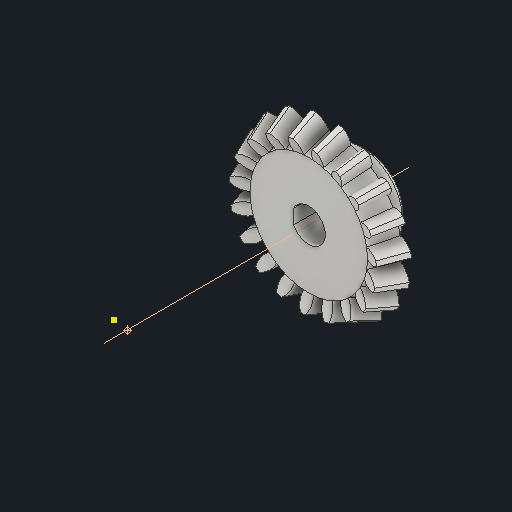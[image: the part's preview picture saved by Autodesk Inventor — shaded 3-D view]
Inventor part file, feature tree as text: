
AUTODESK INVENTOR PART (.ipt)
format: ipt  version: 2022 (Build 260153000, 153)  size: 597,504 bytes
history: native  units: mm
features: other x24, sketch x5, extrude x3, loft x2, pattern_circular x2, chamfer x1
ambient origin geometry x6: Origin, XZ Plane, X Axis, Y Axis, Z Axis, Center Point
bodies: Solid1 (feature_tree)
feature tree (37):
  other  "Top Point"
  other  "Mesh Plane2"
  other  "Teeth Body"
  other  "Start Point"
  other  "Tooth Plane"
  other  "Start Sketch"
  other  "End Point"
  other  "3D Sketch Right"
  other  "End Plane Right"
  loft  "Loft Right"
  pattern_circular  "Circular Pattern Right"  [2 undecoded]
  other  "3D Sketch Left"
  other  "End Plane Left"
  loft  "Loft Left"
  pattern_circular  "Circular Pattern Left"  [2 undecoded]
  other  "Fix Body"
  extrude  "Extrusion1"  Depth=10.0mm
  extrude  "Extrusion2"  Depth=10.0mm
  chamfer  "Chamfer1"  Distance=7.120149mm
  extrude  "Extrusion3"  Depth=10.0mm
  sketch  "Sketch11"  dims[d5=90.0deg d7=6.612538mm d8=8.167518mm d9=22.385367mm d11=8.275mm d12=5.764574mm d15=7.120149mm d16=19.514761mm d17=0.0mm d18=90.0deg d19=0.0mm d20=90.0deg d21=190.0mm d22=360.0deg d26=357.584802mm d27=7.69415mm d28=47.5mm d29=-3.769093mm d30=5.764574mm d31=7.120149mm d32=19.514761mm d35=0.0mm d37=0.0mm d39=0.0mm d40=90.0deg d41=190.0mm d42=360.0deg d46=90.0deg d47=90.0deg d48=0.0mm d49=0.0mm d50=90.0deg d51=1.65347mm d52=0.0mm d53=0.0mm d54=0.0mm d56=20.521955mm d57=28.746717mm d58=20.936717mm d59=25.060358mm d60=18.25188mm d61=25.060358mm d62=18.25188mm d65=357.584802mm d66=31.5mm d67=47.5mm d68=-3.769093mm d69=7.69415mm d70=7.120149mm d71=19.514761mm d72=5.764574mm d73=18.25188mm d74=25.060358mm d75=0.0mm d77=0.0mm d79=0.0mm d80=90.0deg d81=190.0mm d82=360.0deg d84=10.0mm d85=20.0mm d86=20.0mm d87=10.0mm d88=0.0mm d89=0.0mm d90=90.0deg d91=90.0deg d92=90.0deg d93=90.0deg d94=25.0mm d95=10.0mm d96=0.0mm d97=10.0mm d98=0.0mm d99=0.0mm d100=2.0mm d101=2.0mm d102=45.0deg d107=10.0mm d108=0.0mm d114=9.5mm]
  other  "Mesh Plane"
  other  "Top Plane"
  other  "Teeth Body Sketch"
  other  "End Plane"
  other  "End Sketch"
  other  "Helical Curve Left"
  other  "End Sketch Left"
  other  "Body Sketch"
  sketch  "Sketch6"  dims[d0=47.5mm d1=40.16154mm]
  other  "Srf1"
  other  "Helical Curve Right"
  other  "End Sketch Right"
  sketch  "Sketch8"  dims[d2=50.389413mm]
  sketch  "Sketch9"  dims[d3=8.0mm]
  sketch  "Sketch10"  dims[d4=59.428137mm]
  other  "Pitch Diameter"
note: 4 required parameter values undecoded (feature->parameter linkage not recoverable at this tier; creation-order binding heuristic only, values carry confidence <= 0.55)
